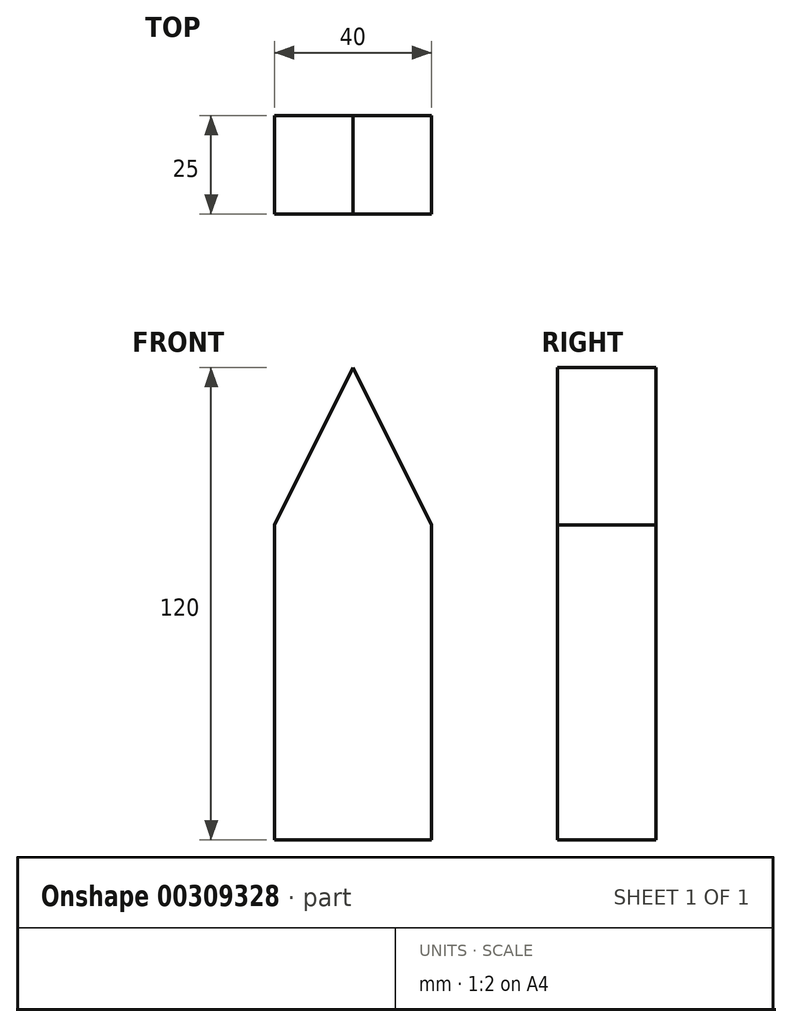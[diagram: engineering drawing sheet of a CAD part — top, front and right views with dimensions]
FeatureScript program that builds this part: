
annotation { "Feature Type Name" : "Feature", "Feature Type Description" : "" }
export const myFeature = defineFeature(function(context is Context, id is Id, definition is map)
    precondition{}
    {
        {
            var Q0;
            Q0=qCreatedBy(makeId("Front.planeOp"),FACE);
            var sketch = newSketch(context, id + "F0", { "sketchPlane" : qUnion([Q0])});
            skLineSegment(sketch, "E0.bottom", {"start": v(20, 40) * mm, "end": v(-20, 40) * mm});
            skLineSegment(sketch, "E0.top", {"start": v(20, -40) * mm, "end": v(-20, -40) * mm});
            skLineSegment(sketch, "E0.left", {"start": v(20, 40) * mm, "end": v(20, -40) * mm});
            skLineSegment(sketch, "E0.right", {"start": v(-20, 40) * mm, "end": v(-20, -40) * mm});
            skPoint(sketch, "E0.middle", {"position": v(0, 0) * mm});
            skLineSegment(sketch, "E1", {"start": v(-20, 40) * mm, "end": v(0, 80) * mm});
            skLineSegment(sketch, "E2", {"start": v(20, 40) * mm, "end": v(0, 80) * mm});
            skSolve(sketch);
        }
        {
            var Q0;
            Q0 = qSketchRegion(id + "F0", true);
            extrude(context, id + "F1", {"entities" : qUnion([Q0]), "depth" : 25 * mm});
        }
    });
